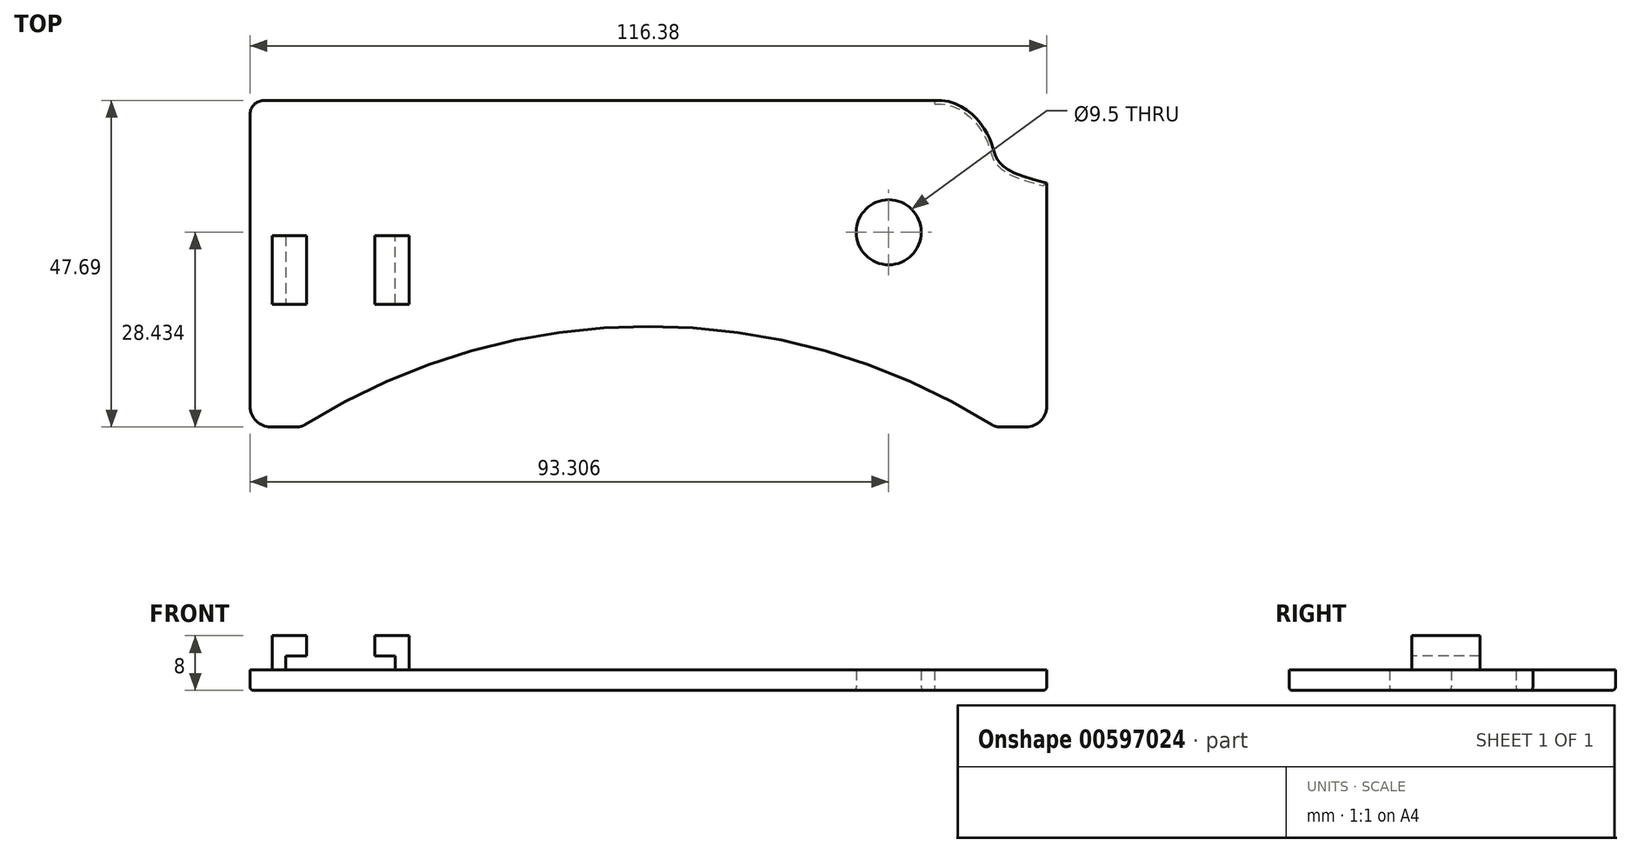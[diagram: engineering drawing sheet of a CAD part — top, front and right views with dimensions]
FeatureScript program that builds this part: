
annotation { "Feature Type Name" : "Feature", "Feature Type Description" : "" }
export const myFeature = defineFeature(function(context is Context, id is Id, definition is map)
    precondition{}
    {
        {
            var Q0;
            Q0=qCreatedBy(makeId("Top.planeOp"),FACE);
            var sketch = newSketch(context, id + "F0", { "sketchPlane" : qUnion([Q0])});
            skLineSegment(sketch, "E0.top", {"start": v(-60.07, 43.77) * mm, "end": v(56.31, 43.77) * mm});
            skLineSegment(sketch, "E0.left", {"start": v(-60.07, 53.81) * mm, "end": v(-60.07, 43.77) * mm});
            skLineSegment(sketch, "E1", {"start": v(-60.07, 43.77) * mm, "end": v(-60.07, 11.15) * mm});
            skLineSegment(sketch, "E2", {"start": v(56.31, 43.77) * mm, "end": v(56.31, 11.15) * mm});
            skLineSegment(sketch, "E3", {"start": v(-57.07, 8.15) * mm, "end": v(-53.12, 8.15) * mm});
            skLineSegment(sketch, "E4", {"start": v(53.31, 8.15) * mm, "end": v(49.36, 8.15) * mm});
            skArc(sketch, "E5", {"start": v(48.3, 8.45) * mm, "mid": v(-1.88, 22.83) * mm, "end": v(-52.06, 8.45) * mm});
            skPoint(sketch, "E6.visualSharp", {"position": v(-60.07, 8.15) * mm});
            skArc(sketch, "E6.filletArc", {"start": v(-60.07, 11.15) * mm, "mid": v(-59.2, 9.03) * mm, "end": v(-57.07, 8.15) * mm});
            skPoint(sketch, "E7.visualSharp", {"position": v(56.31, 8.15) * mm});
            skArc(sketch, "E7.filletArc", {"start": v(53.31, 8.15) * mm, "mid": v(55.43, 9.03) * mm, "end": v(56.31, 11.15) * mm});
            skPoint(sketch, "E8.visualSharp", {"position": v(-60.07, 55.81) * mm});
            skArc(sketch, "E8.filletArc", {"start": v(-58.07, 55.81) * mm, "mid": v(-59.49, 55.23) * mm, "end": v(-60.07, 53.81) * mm});
            skPoint(sketch, "E9.visualSharp", {"position": v(-52.55, 8.15) * mm});
            skArc(sketch, "E9.filletArc", {"start": v(-53.12, 8.15) * mm, "mid": v(-52.57, 8.23) * mm, "end": v(-52.06, 8.45) * mm});
            skPoint(sketch, "E10.visualSharp", {"position": v(48.78, 8.15) * mm});
            skArc(sketch, "E10.filletArc", {"start": v(48.3, 8.45) * mm, "mid": v(48.8, 8.23) * mm, "end": v(49.36, 8.15) * mm});
            skCircle(sketch, "E11", {"center": v(33.24, 36.58) * mm, "radius": 4.75 * mm});
            skLineSegment(sketch, "E12.bottom", {"start": v(-56.84, 36.06) * mm, "end": v(-36.84, 36.06) * mm});
            skLineSegment(sketch, "E12.top", {"start": v(-56.84, 26.06) * mm, "end": v(-36.84, 26.06) * mm});
            skLineSegment(sketch, "E12.left", {"start": v(-56.84, 36.06) * mm, "end": v(-56.84, 26.06) * mm});
            skLineSegment(sketch, "E12.right", {"start": v(-36.84, 36.06) * mm, "end": v(-36.84, 26.06) * mm});
            skLineSegment(sketch, "E13", {"start": v(-54.84, 36.06) * mm, "end": v(-54.84, 26.06) * mm});
            skLineSegment(sketch, "E14", {"start": v(-38.84, 26.06) * mm, "end": v(-38.84, 36.06) * mm});
            skLineSegment(sketch, "E15", {"start": v(-51.84, 36.06) * mm, "end": v(-51.84, 26.06) * mm});
            skLineSegment(sketch, "E16", {"start": v(-41.84, 36.06) * mm, "end": v(-41.84, 26.06) * mm});
            skLineSegment(sketch, "E17", {"start": v(-58.07, 55.81) * mm, "end": v(39.93, 55.81) * mm});
            skFitSpline(sketch, "E18", {"points": [v(39.93, 55.81) * mm, v(48.13, 49.94) * mm, v(56.31, 43.77) * mm], "startDerivative": vector(24.76, 2.42) * mm, "endDerivative": vector(48.88, -11.84) * mm});
            skSolve(sketch);
        }
        {
            var Q0;
            {var subQ1=sQuery(id+"F0.wireOp",EDGE,"E0.left");Q0=makeQuery(id+"F0.imprint","IMPRINT",FACE,{"disambiguationData":[TD([[makeQuery(id+"F0.imprint","IMPRINT",EDGE,{"derivedFrom":subQ1}),1.0]])]});}
            var Q1;
            {var subQ1=sQuery(id+"F0.wireOp",EDGE,"E1");Q1=makeQuery(id+"F0.imprint","IMPRINT",FACE,{"disambiguationData":[TD([[makeQuery(id+"F0.imprint","IMPRINT",EDGE,{"derivedFrom":subQ1}),1.0]])]});}
            var Q2;
            {var subQ0=sQuery(id+"F0.wireOp",EDGE,"E13");Q2=makeQuery(id+"F0.imprint","IMPRINT",FACE,{"disambiguationData":[TD([[makeQuery(id+"F0.imprint","IMPRINT",EDGE,{"derivedFrom":subQ0}),1.0]])]});}
            var Q3;
            {var subQ0=sQuery(id+"F0.wireOp",EDGE,"E12.left");Q3=makeQuery(id+"F0.imprint","IMPRINT",FACE,{"disambiguationData":[TD([[makeQuery(id+"F0.imprint","IMPRINT",EDGE,{"derivedFrom":subQ0}),1.0]])]});}
            var Q4;
            {var subQ0=sQuery(id+"F0.wireOp",EDGE,"E15");Q4=makeQuery(id+"F0.imprint","IMPRINT",FACE,{"disambiguationData":[TD([[makeQuery(id+"F0.imprint","IMPRINT",EDGE,{"derivedFrom":subQ0}),1.0]])]});}
            var Q5;
            {var subQ0=sQuery(id+"F0.wireOp",EDGE,"E14");Q5=makeQuery(id+"F0.imprint","IMPRINT",FACE,{"disambiguationData":[TD([[makeQuery(id+"F0.imprint","IMPRINT",EDGE,{"derivedFrom":subQ0}),1.0]])]});}
            var Q6;
            {var subQ0=sQuery(id+"F0.wireOp",EDGE,"E12.right");Q6=makeQuery(id+"F0.imprint","IMPRINT",FACE,{"disambiguationData":[TD([[makeQuery(id+"F0.imprint","IMPRINT",EDGE,{"derivedFrom":subQ0}),-1.0]])]});}
            extrude(context, id + "F1", {"entities" : qUnion([Q0, Q1, Q2, Q3, Q4, Q5, Q6]), "depth" : 3 * mm, "offsetDistance" : 25 * mm});
        }
        {
            var Q0;
            {var subQ0=sQuery(id+"F0.wireOp",EDGE,"E12.left");Q0=makeQuery(id+"F0.imprint","IMPRINT",FACE,{"disambiguationData":[TD([[makeQuery(id+"F0.imprint","IMPRINT",EDGE,{"derivedFrom":subQ0}),1.0]])]});}
            var Q1;
            {var subQ0=sQuery(id+"F0.wireOp",EDGE,"E12.right");Q1=makeQuery(id+"F0.imprint","IMPRINT",FACE,{"disambiguationData":[TD([[makeQuery(id+"F0.imprint","IMPRINT",EDGE,{"derivedFrom":subQ0}),-1.0]])]});}
            extrude(context, id + "F2", {"entities" : qUnion([Q0, Q1]), "operationType" : NewBodyOperationType.ADD, "depth" : 5.5 * mm, "offsetDistance" : 25 * mm});
        }
        {
            var Q0;
            {var subQ0=sQuery(id+"F0.wireOp",EDGE,"E12.left");Q0=makeQuery(id+"F0.imprint","IMPRINT",FACE,{"disambiguationData":[TD([[makeQuery(id+"F0.imprint","IMPRINT",EDGE,{"derivedFrom":subQ0}),1.0]])]});}
            var Q1;
            {var subQ0=sQuery(id+"F0.wireOp",EDGE,"E13");Q1=makeQuery(id+"F0.imprint","IMPRINT",FACE,{"disambiguationData":[TD([[makeQuery(id+"F0.imprint","IMPRINT",EDGE,{"derivedFrom":subQ0}),1.0]])]});}
            var Q2;
            {var subQ0=sQuery(id+"F0.wireOp",EDGE,"E14");Q2=makeQuery(id+"F0.imprint","IMPRINT",FACE,{"disambiguationData":[TD([[makeQuery(id+"F0.imprint","IMPRINT",EDGE,{"derivedFrom":subQ0}),1.0]])]});}
            var Q3;
            {var subQ0=sQuery(id+"F0.wireOp",EDGE,"E12.right");Q3=makeQuery(id+"F0.imprint","IMPRINT",FACE,{"disambiguationData":[TD([[makeQuery(id+"F0.imprint","IMPRINT",EDGE,{"derivedFrom":subQ0}),-1.0]])]});}
            extrude(context, id + "F3", {"entities" : qUnion([Q0, Q1, Q2, Q3]), "operationType" : NewBodyOperationType.ADD, "depth" : 8 * mm, "hasOffset" : true, "offsetDistance" : 25 * mm, "hasSecondDirection" : true, "secondDirectionOppositeDirection" : false, "secondDirectionDepth" : 5 * mm});
        }
        {
            var Q0;
            Q0=makeQuery(id+"F1.opExtrude","CAP_EDGE",EDGE,{"disambiguationData":[OSD([sQuery(id+"F0.wireOp",EDGE,"E17")])],"isStart":true});
            var Q1;
            Q1=makeQuery(id+"F1.opExtrude","CAP_EDGE",EDGE,{"disambiguationData":[OSD([sQuery(id+"F0.wireOp",EDGE,"E18")])],"isStart":true});
            var Q2;
            Q2=makeQuery(id+"F1.opExtrude","CAP_EDGE",EDGE,{"disambiguationData":[OSD([sQuery(id+"F0.wireOp",EDGE,"E11")])],"isStart":true});
            fillet(context, id + "F4", {"entities" : qUnion([Q0, Q1, Q2]), "radius" : 0.5 * mm, "tangentPropagation" : true, "allowEdgeOverflow" : false});
        }
    });
